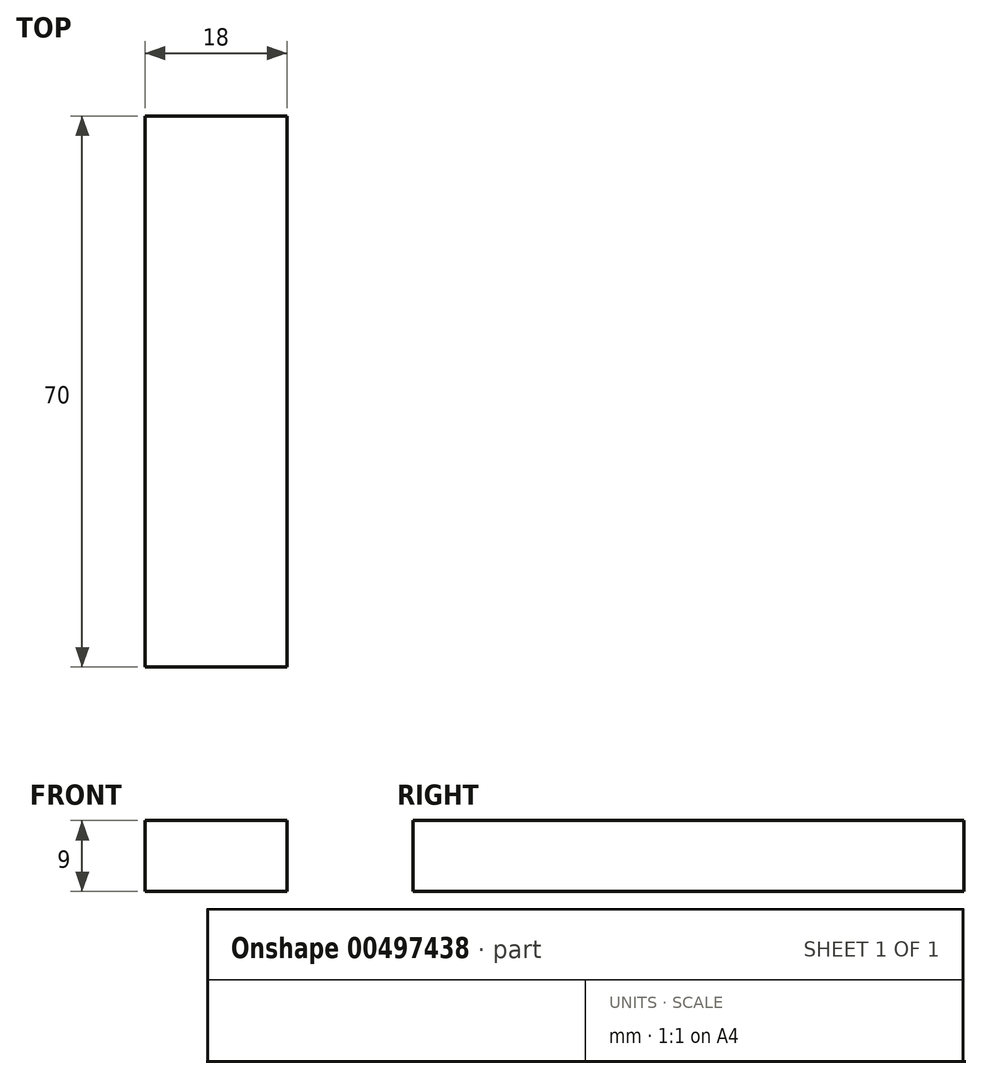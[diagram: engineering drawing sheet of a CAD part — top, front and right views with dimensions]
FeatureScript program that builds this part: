
annotation { "Feature Type Name" : "Feature", "Feature Type Description" : "" }
export const myFeature = defineFeature(function(context is Context, id is Id, definition is map)
    precondition{}
    {
        {
            var Q0;
            Q0=qCreatedBy(makeId("Front.planeOp"),FACE);
            var sketch = newSketch(context, id + "F0", { "sketchPlane" : qUnion([Q0])});
            skLineSegment(sketch, "E0.bottom", {"start": v(9, -4.5) * mm, "end": v(-9, -4.5) * mm});
            skLineSegment(sketch, "E0.top", {"start": v(9, 4.5) * mm, "end": v(-9, 4.5) * mm});
            skLineSegment(sketch, "E0.left", {"start": v(9, -4.5) * mm, "end": v(9, 4.5) * mm});
            skLineSegment(sketch, "E0.right", {"start": v(-9, -4.5) * mm, "end": v(-9, 4.5) * mm});
            skPoint(sketch, "E0.middle", {"position": v(0, 0) * mm});
            skSolve(sketch);
        }
        {
            var Q0;
            Q0 = qSketchRegion(id + "F0", true);
            extrude(context, id + "F1", {"entities" : qUnion([Q0]), "depth" : 70 * mm});
        }
    });
